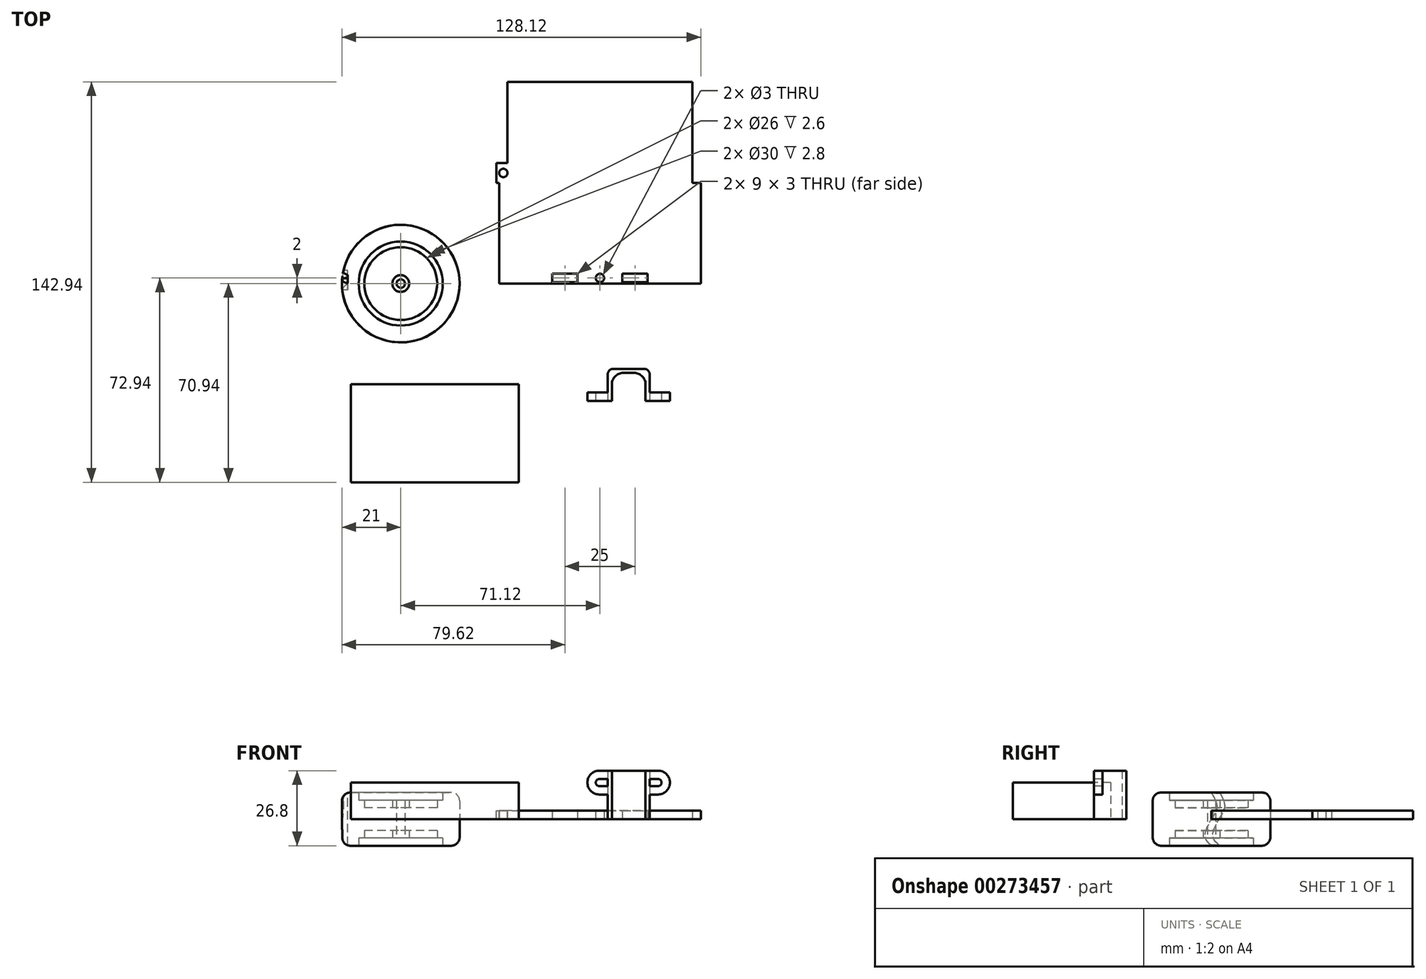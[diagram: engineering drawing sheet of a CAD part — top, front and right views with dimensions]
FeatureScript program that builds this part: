
annotation { "Feature Type Name" : "Feature", "Feature Type Description" : "" }
export const myFeature = defineFeature(function(context is Context, id is Id, definition is map)
    precondition{}
    {
        {
            var Q0;
            Q0=qCreatedBy(makeId("Top.planeOp"),FACE);
            var sketch = newSketch(context, id + "F0", { "sketchPlane" : qUnion([Q0])});
            skLineSegment(sketch, "E0", {"start": v(0, 0) * mm, "end": v(53.12, 0) * mm});
            skLineSegment(sketch, "E1", {"start": v(53.12, 0) * mm, "end": v(53.12, 36) * mm});
            skLineSegment(sketch, "E2", {"start": v(53.12, 36) * mm, "end": v(50.12, 36) * mm});
            skLineSegment(sketch, "E3", {"start": v(50.12, 36) * mm, "end": v(50.12, 72) * mm});
            skLineSegment(sketch, "E4", {"start": v(50.12, 72) * mm, "end": v(-15.88, 72) * mm});
            skLineSegment(sketch, "E5", {"start": v(-15.88, 72) * mm, "end": v(-15.88, 36) * mm});
            skLineSegment(sketch, "E6", {"start": v(-15.88, 36) * mm, "end": v(-18.88, 36) * mm});
            skLineSegment(sketch, "E7", {"start": v(-18.88, 36) * mm, "end": v(-18.88, 0) * mm});
            skLineSegment(sketch, "E8", {"start": v(-18.88, 0) * mm, "end": v(0, 0) * mm});
            skCircle(sketch, "E9", {"center": v(17.12, 2) * mm, "radius": 1.5 * mm});
            skLineSegment(sketch, "E10.bottom", {"start": v(25.12, 3.5) * mm, "end": v(34.12, 3.5) * mm});
            skLineSegment(sketch, "E10.top", {"start": v(25.12, 0.5) * mm, "end": v(34.12, 0.5) * mm});
            skLineSegment(sketch, "E10.left", {"start": v(25.12, 3.5) * mm, "end": v(25.12, 0.5) * mm});
            skLineSegment(sketch, "E10.right", {"start": v(34.12, 3.5) * mm, "end": v(34.12, 0.5) * mm});
            skLineSegment(sketch, "E11", {"start": v(17.12, 2) * mm, "end": v(17.12, 11.74) * mm, "construction": true});
            skLineSegment(sketch, "E12.MirrorCS", {"start": v(0.12, 3.5) * mm, "end": v(0.12, 0.5) * mm});
            skLineSegment(sketch, "E13.MirrorCS", {"start": v(9.12, 3.5) * mm, "end": v(0.12, 3.5) * mm});
            skLineSegment(sketch, "E14.MirrorCS", {"start": v(9.12, 0.5) * mm, "end": v(0.12, 0.5) * mm});
            skLineSegment(sketch, "E15.MirrorCS", {"start": v(9.12, 3.5) * mm, "end": v(9.12, 0.5) * mm});
            skSolve(sketch);
        }
        {
            var Q0;
            Q0=makeQuery(id+"F0.imprint","IMPRINT",FACE,{"disambiguationData":[TD([[makeQuery(id+"F0.imprint","IMPRINT",EDGE,{"derivedFrom":sQuery(id+"F0.wireOp",EDGE,"E0")}),1.0]])]});
            extrude(context, id + "F1", {"entities" : qUnion([Q0]), "depth" : 3 * mm});
        }
        {
            var Q0;
            Q0=makeQuery(id+"F1.opExtrude","CAP_FACE",FACE,{"disambiguationData":[OSD([sQuery(id+"F0.wireOp",EDGE,"E0"),sQuery(id+"F0.wireOp",EDGE,"E1"),sQuery(id+"F0.wireOp",EDGE,"E2"),sQuery(id+"F0.wireOp",EDGE,"E3"),sQuery(id+"F0.wireOp",EDGE,"E4"),sQuery(id+"F0.wireOp",EDGE,"E5"),sQuery(id+"F0.wireOp",EDGE,"E6"),sQuery(id+"F0.wireOp",EDGE,"E7"),sQuery(id+"F0.wireOp",EDGE,"E8")])],"isStart":false});
            var sketch = newSketch(context, id + "F2", { "sketchPlane" : qUnion([Q0])});
            skLineSegment(sketch, "E16", {"start": v(-15.88, 43) * mm, "end": v(-19.88, 43) * mm});
            skLineSegment(sketch, "E17", {"start": v(-19.88, 43) * mm, "end": v(-19.88, 36) * mm});
            skLineSegment(sketch, "E18", {"start": v(-19.88, 36) * mm, "end": v(-15.88, 36) * mm});
            skCircle(sketch, "E19", {"center": v(-17.38, 39.5) * mm, "radius": 1.5 * mm});
            skSolve(sketch);
        }
        {
            var Q0;
            {var subQ0=sQuery(id+"F2.wireOp",EDGE,"E16");Q0=makeQuery(id+"F2.imprint","IMPRINT",FACE,{"disambiguationData":[TD([[makeQuery(id+"F2.imprint","IMPRINT",EDGE,{"derivedFrom":subQ0}),1.0]])]});}
            var Q1;
            {var subQ0=sQuery(id+"F2.wireOp",EDGE,"IvL0JwNL-QslB-qBAy-HYgE-RIXDcQyQFNQj");Q1=makeQuery(id+"F2.imprint","IMPRINT",FACE,{"disambiguationData":[TD([[makeQuery(id+"F2.imprint","IMPRINT",EDGE,{"derivedFrom":subQ0}),1.0]])]});}
            var Q2;
            {var subQ0=sQuery(id+"F2.wireOp",EDGE,"E18");Q2=makeQuery(id+"F2.imprint","IMPRINT",FACE,{"disambiguationData":[TD([[makeQuery(id+"F2.imprint","IMPRINT",EDGE,{"derivedFrom":subQ0}),1.0]])]});}
            extrude(context, id + "F3", {"entities" : qUnion([Q0, Q1, Q2]), "operationType" : NewBodyOperationType.ADD, "oppositeDirection" : true, "depth" : 3 * mm});
        }
        {
            var Q0;
            Q0=makeQuery(id+"F1.opExtrude","SWEPT_FACE",FACE,{"disambiguationData":[OSD([sQuery(id+"F0.wireOp",EDGE,"E7")])]});
            cPlane(context, id + "F4", {"entities" : qUnion([Q0]), "cplaneType" : CPlaneType.OFFSET, "offset" : 36 * mm, "oppositeDirection" : true, "width" : 150 * mm, "height" : 150 * mm});
        }
        {
            var Q0;
            Q0=qCreatedBy(makeId("Top.planeOp"),FACE);
            var sketch = newSketch(context, id + "F5", { "sketchPlane" : qUnion([Q0])});
            skCircle(sketch, "E20", {"center": v(-54, 0) * mm, "radius": 21 * mm});
            skCircle(sketch, "E21", {"center": v(-54, 0) * mm, "radius": 15 * mm});
            skCircle(sketch, "E22", {"center": v(-54, 0) * mm, "radius": 13 * mm});
            skCircle(sketch, "E23", {"center": v(-54, 0) * mm, "radius": 3 * mm});
            skCircle(sketch, "E24", {"center": v(-54, 0) * mm, "radius": 1.5 * mm});
            skLineSegment(sketch, "E25", {"start": v(0, 0) * mm, "end": v(-75, 0) * mm, "construction": true});
            skLineSegment(sketch, "E26", {"start": v(-75, 0) * mm, "end": v(-75, 25.36) * mm, "construction": true});
            skSolve(sketch);
        }
        {
            var Q0;
            Q0=makeQuery(id+"F5.imprint","IMPRINT",FACE,{"disambiguationData":[TD([[makeQuery(id+"F5.imprint","IMPRINT",EDGE,{"derivedFrom":sQuery(id+"F5.wireOp",EDGE,"E20")}),1.0]])]});
            extrude(context, id + "F6", {"entities" : qUnion([Q0]), "endBound" : BoundingType.SYMMETRIC, "depth" : 19 * mm});
        }
        {
            var Q0;
            Q0=makeQuery(id+"F5.imprint","IMPRINT",FACE,{"disambiguationData":[TD([[makeQuery(id+"F5.imprint","IMPRINT",EDGE,{"derivedFrom":sQuery(id+"F5.wireOp",EDGE,"E21")}),1.0]])]});
            extrude(context, id + "F7", {"entities" : qUnion([Q0]), "operationType" : NewBodyOperationType.ADD, "endBound" : BoundingType.SYMMETRIC, "depth" : 13.4 * mm});
        }
        {
            var Q0;
            Q0=makeQuery(id+"F5.imprint","IMPRINT",FACE,{"disambiguationData":[TD([[makeQuery(id+"F5.imprint","IMPRINT",EDGE,{"derivedFrom":sQuery(id+"F5.wireOp",EDGE,"E22")}),1.0]])]});
            extrude(context, id + "F8", {"entities" : qUnion([Q0]), "operationType" : NewBodyOperationType.ADD, "endBound" : BoundingType.SYMMETRIC, "depth" : 8.2 * mm});
        }
        {
            var Q0;
            Q0=makeQuery(id+"F5.imprint","IMPRINT",FACE,{"disambiguationData":[TD([[makeQuery(id+"F5.imprint","IMPRINT",EDGE,{"derivedFrom":sQuery(id+"F5.wireOp",EDGE,"E23")}),1.0]])]});
            extrude(context, id + "F9", {"entities" : qUnion([Q0]), "operationType" : NewBodyOperationType.ADD, "endBound" : BoundingType.SYMMETRIC, "depth" : 13.4 * mm});
        }
        {
            var Q0;
            Q0=qCreatedBy(makeId("Right.planeOp"),FACE);
            cPlane(context, id + "F10", {"entities" : qUnion([Q0]), "cplaneType" : CPlaneType.OFFSET, "offset" : 75 * mm, "oppositeDirection" : true, "width" : 150 * mm, "height" : 150 * mm});
        }
        {
            var Q0;
            Q0=qCreatedBy(id+"F10.planeOp",FACE);
            var sketch = newSketch(context, id + "F11", { "sketchPlane" : qUnion([Q0])});
            skLineSegment(sketch, "E27", {"start": v(0, 0) * mm, "end": v(0, 9.5) * mm, "construction": true});
            skLineSegment(sketch, "E28", {"start": v(0, 0) * mm, "end": v(0, -9.5) * mm, "construction": true});
            skFitSpline(sketch, "E29", {"points": [v(0, -9.5) * mm, v(-2.3, -6.2) * mm, v(0, 0) * mm, v(1.96, 4.37) * mm, v(0, 9.5) * mm], "startDerivative": vector(-14.6, 13.01) * mm, "endDerivative": vector(-11.63, 20.83) * mm});
            skFitSpline(sketch, "E30", {"points": [v(3, -9.5) * mm, v(0.47, -6.08) * mm, v(2.76, 0.12) * mm, v(4.73, 4.49) * mm, v(3, 9.5) * mm], "startDerivative": vector(-14.6, 13.01) * mm, "endDerivative": vector(-11.63, 20.83) * mm});
            skLineSegment(sketch, "E31", {"start": v(3, -9.5) * mm, "end": v(0, -9.5) * mm});
            skLineSegment(sketch, "E32", {"start": v(3, 9.5) * mm, "end": v(0, 9.5) * mm});
            skSolve(sketch);
        }
        {
            var Q0;
            Q0=makeQuery(id+"F6.opExtrude","CAP_EDGE",EDGE,{"disambiguationData":[OSD([sQuery(id+"F5.wireOp",EDGE,"E20")])],"isStart":false});
            var Q1;
            Q1=makeQuery(id+"F6.opExtrude","CAP_EDGE",EDGE,{"disambiguationData":[OSD([sQuery(id+"F5.wireOp",EDGE,"E20")])],"isStart":true});
            fillet(context, id + "F12", {"entities" : qUnion([Q0, Q1]), "radius" : 3 * mm, "tangentPropagation" : true, "allowEdgeOverflow" : false});
        }
        {
            var Q0;
            Q0=makeQuery(id+"F11.imprint","IMPRINT",FACE,{"disambiguationData":[TD([[makeQuery(id+"F11.imprint","IMPRINT",EDGE,{"derivedFrom":sQuery(id+"F11.wireOp",EDGE,"E29")}),-1.0]])]});
            extrude(context, id + "F13", {"entities" : qUnion([Q0]), "operationType" : NewBodyOperationType.REMOVE, "depth" : 2 * mm});
        }
        {
            var Q0;
            Q0=qCreatedBy(makeId("Top.planeOp"),FACE);
            var sketch = newSketch(context, id + "F14", { "sketchPlane" : qUnion([Q0])});
            skLineSegment(sketch, "E33.bottom", {"start": v(21.88, -30.42) * mm, "end": v(32.88, -30.42) * mm});
            skLineSegment(sketch, "E33.top", {"start": v(19.88, -41.92) * mm, "end": v(34.88, -41.92) * mm});
            skLineSegment(sketch, "E33.left", {"start": v(19.88, -32.42) * mm, "end": v(19.88, -41.92) * mm});
            skLineSegment(sketch, "E33.right", {"start": v(34.88, -32.42) * mm, "end": v(34.88, -41.92) * mm});
            skLineSegment(sketch, "E34.bottom", {"start": v(21.38, -41.92) * mm, "end": v(33.38, -41.92) * mm});
            skLineSegment(sketch, "E34.top", {"start": v(25.38, -31.92) * mm, "end": v(29.38, -31.92) * mm});
            skLineSegment(sketch, "E34.left", {"start": v(21.38, -41.92) * mm, "end": v(21.38, -35.92) * mm});
            skLineSegment(sketch, "E34.right", {"start": v(33.38, -41.92) * mm, "end": v(33.38, -35.92) * mm});
            skPoint(sketch, "E35.visualSharp", {"position": v(21.38, -31.92) * mm});
            skArc(sketch, "E35.filletArc", {"start": v(25.38, -31.92) * mm, "mid": v(22.55, -33.1) * mm, "end": v(21.38, -35.92) * mm});
            skPoint(sketch, "E36.visualSharp", {"position": v(33.38, -31.92) * mm});
            skArc(sketch, "E36.filletArc", {"start": v(33.38, -35.92) * mm, "mid": v(32.2, -33.1) * mm, "end": v(29.38, -31.92) * mm});
            skPoint(sketch, "E37.visualSharp", {"position": v(19.88, -30.42) * mm});
            skArc(sketch, "E37.filletArc", {"start": v(21.88, -30.42) * mm, "mid": v(20.46, -31) * mm, "end": v(19.88, -32.42) * mm});
            skPoint(sketch, "E38.visualSharp", {"position": v(34.88, -30.42) * mm});
            skArc(sketch, "E38.filletArc", {"start": v(34.88, -32.42) * mm, "mid": v(34.3, -31) * mm, "end": v(32.88, -30.42) * mm});
            skSolve(sketch);
        }
        {
            var Q0;
            Q0=makeQuery(id+"F14.imprint","IMPRINT",FACE,{"disambiguationData":[TD([[makeQuery(id+"F14.imprint","IMPRINT",EDGE,{"derivedFrom":sQuery(id+"F14.wireOp",EDGE,"E33.bottom")}),-1.0]])]});
            extrude(context, id + "F15", {"entities" : qUnion([Q0]), "depth" : 17.3 * mm});
        }
        {
            var Q0;
            {var subQ0=sQuery(id+"F14.wireOp",EDGE,"E33.top");Q0=makeQuery(id+"F15.opExtrude","SWEPT_FACE",FACE,{"disambiguationData":[OSD([subQ0]),TDD([makeQuery(id+"F14.imprint","IMPRINT",EDGE,{"disambiguationData":[TD([[makeQuery(id+"F14.imprint","INTERSECT",VERTEX,{"derivedFrom":[subQ0,sQuery(id+"F14.wireOp",EDGE,"E33.right")]}),1.0]])],"derivedFrom":subQ0})])]});}
            var sketch = newSketch(context, id + "F16", { "sketchPlane" : qUnion([Q0])});
            skLineSegment(sketch, "E39", {"start": v(34.88, 17.3) * mm, "end": v(34.88, 14.3) * mm});
            skLineSegment(sketch, "E40", {"start": v(34.88, 17.3) * mm, "end": v(37.88, 17.3) * mm});
            skArc(sketch, "E41", {"start": v(37.88, 8.8) * mm, "mid": v(42.13, 13.05) * mm, "end": v(37.88, 17.3) * mm});
            skArc(sketch, "E42", {"start": v(37.88, 11.8) * mm, "mid": v(39.13, 13.05) * mm, "end": v(37.88, 14.3) * mm});
            skLineSegment(sketch, "E43", {"start": v(37.88, 14.3) * mm, "end": v(34.88, 14.3) * mm});
            skLineSegment(sketch, "E44", {"start": v(37.88, 11.8) * mm, "end": v(34.88, 11.8) * mm});
            skLineSegment(sketch, "E45", {"start": v(34.88, 11.8) * mm, "end": v(34.88, 8.8) * mm});
            skLineSegment(sketch, "E46", {"start": v(37.88, 8.8) * mm, "end": v(34.88, 8.8) * mm});
            skLineSegment(sketch, "E47", {"start": v(34.88, 17.3) * mm, "end": v(27.38, 17.3) * mm});
            skLineSegment(sketch, "E48", {"start": v(27.38, 17.3) * mm, "end": v(27.38, 11.08) * mm, "construction": true});
            skLineSegment(sketch, "E49.MirrorCS", {"start": v(19.88, 17.3) * mm, "end": v(27.38, 17.3) * mm});
            skLineSegment(sketch, "E50.MirrorCS", {"start": v(19.88, 17.3) * mm, "end": v(19.88, 14.3) * mm});
            skLineSegment(sketch, "E51.MirrorCS", {"start": v(16.88, 14.3) * mm, "end": v(19.88, 14.3) * mm});
            skLineSegment(sketch, "E52.MirrorCS", {"start": v(19.88, 11.8) * mm, "end": v(19.88, 8.8) * mm});
            skArc(sketch, "E53.MirrorCS", {"start": v(16.88, 11.8) * mm, "mid": v(15.63, 13.05) * mm, "end": v(16.88, 14.3) * mm});
            skLineSegment(sketch, "E54.MirrorCS", {"start": v(16.88, 11.8) * mm, "end": v(19.88, 11.8) * mm});
            skLineSegment(sketch, "E55.MirrorCS", {"start": v(16.88, 8.8) * mm, "end": v(19.88, 8.8) * mm});
            skArc(sketch, "E56.MirrorCS", {"start": v(16.88, 8.8) * mm, "mid": v(12.63, 13.05) * mm, "end": v(16.88, 17.3) * mm});
            skLineSegment(sketch, "E57.MirrorCS", {"start": v(19.88, 17.3) * mm, "end": v(16.88, 17.3) * mm});
            skSolve(sketch);
        }
        {
            var Q0;
            Q0=makeQuery(id+"F16.imprint","IMPRINT",FACE,{"disambiguationData":[TD([[makeQuery(id+"F16.imprint","IMPRINT",EDGE,{"derivedFrom":sQuery(id+"F16.wireOp",EDGE,"E39")}),1.0]])]});
            var Q1;
            Q1=makeQuery(id+"F16.imprint","IMPRINT",FACE,{"disambiguationData":[TD([[makeQuery(id+"F16.imprint","IMPRINT",EDGE,{"derivedFrom":sQuery(id+"F16.wireOp",EDGE,"E50.MirrorCS")}),-1.0]])]});
            extrude(context, id + "F17", {"entities" : qUnion([Q0, Q1]), "operationType" : NewBodyOperationType.ADD, "oppositeDirection" : true, "depth" : 3 * mm});
        }
        {
            var Q0;
            Q0=qCreatedBy(makeId("Top.planeOp"),FACE);
            var sketch = newSketch(context, id + "F18", { "sketchPlane" : qUnion([Q0])});
            skLineSegment(sketch, "E58.bottom", {"start": v(-71.85, -35.94) * mm, "end": v(-11.85, -35.94) * mm});
            skLineSegment(sketch, "E58.top", {"start": v(-71.85, -70.94) * mm, "end": v(-11.85, -70.94) * mm});
            skLineSegment(sketch, "E58.left", {"start": v(-71.85, -35.94) * mm, "end": v(-71.85, -70.94) * mm});
            skLineSegment(sketch, "E58.right", {"start": v(-11.85, -35.94) * mm, "end": v(-11.85, -70.94) * mm});
            skSolve(sketch);
        }
        {
            var Q0;
            Q0=makeQuery(id+"F18.imprint","IMPRINT",FACE,{"disambiguationData":[TD([[makeQuery(id+"F18.imprint","IMPRINT",EDGE,{"derivedFrom":sQuery(id+"F18.wireOp",EDGE,"E58.bottom")}),-1.0]])]});
            extrude(context, id + "F19", {"entities" : qUnion([Q0]), "depth" : 13 * mm});
        }
    });
